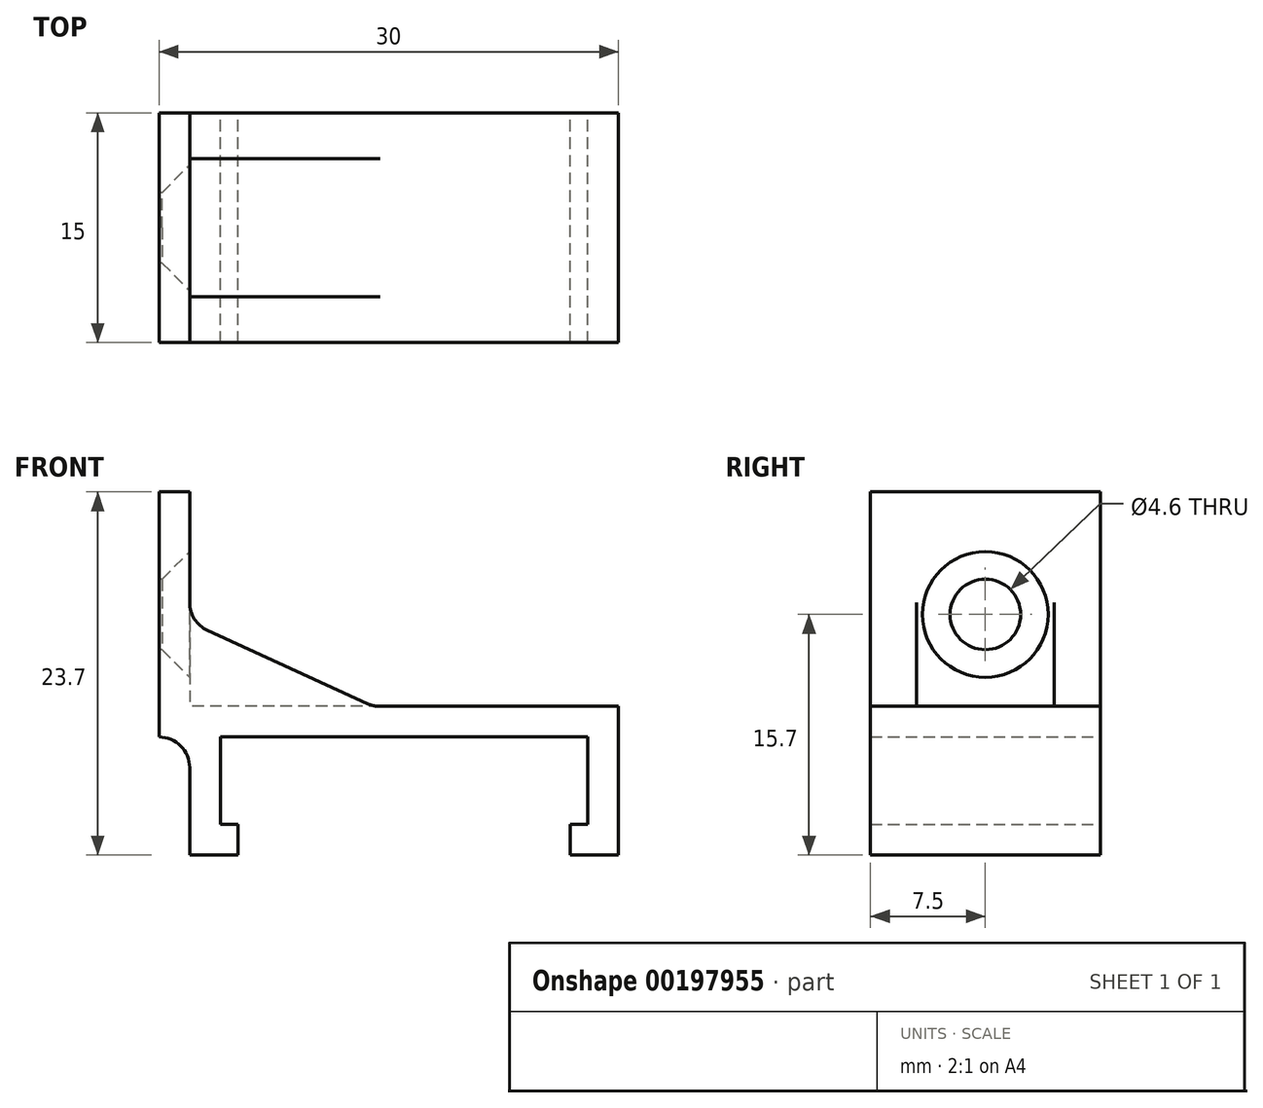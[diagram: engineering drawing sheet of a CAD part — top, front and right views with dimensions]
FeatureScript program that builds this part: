
annotation { "Feature Type Name" : "Feature", "Feature Type Description" : "" }
export const myFeature = defineFeature(function(context is Context, id is Id, definition is map)
    precondition{}
    {
        {
            var Q0;
            Q0=qCreatedBy(makeId("Front.planeOp"),FACE);
            var sketch = newSketch(context, id + "F0", { "sketchPlane" : qUnion([Q0])});
            skLineSegment(sketch, "E0", {"start": v(0, 16) * mm, "end": v(0, 0) * mm});
            skLineSegment(sketch, "E1", {"start": v(2, 0) * mm, "end": v(2, -7.7) * mm});
            skLineSegment(sketch, "E2", {"start": v(2, -7.7) * mm, "end": v(5.15, -7.7) * mm});
            skLineSegment(sketch, "E3", {"start": v(5.15, -7.7) * mm, "end": v(5.15, -5.7) * mm});
            skLineSegment(sketch, "E4", {"start": v(5.15, -5.7) * mm, "end": v(4, -5.7) * mm});
            skLineSegment(sketch, "E5", {"start": v(4, -5.7) * mm, "end": v(4, 0) * mm});
            skLineSegment(sketch, "E6", {"start": v(4, 0) * mm, "end": v(28, 0) * mm});
            skLineSegment(sketch, "E7", {"start": v(28, 0) * mm, "end": v(28, -5.7) * mm});
            skLineSegment(sketch, "E8", {"start": v(28, -5.7) * mm, "end": v(26.85, -5.7) * mm});
            skLineSegment(sketch, "E9", {"start": v(26.85, -5.7) * mm, "end": v(26.85, -7.7) * mm});
            skLineSegment(sketch, "E10", {"start": v(26.85, -7.7) * mm, "end": v(30, -7.7) * mm});
            skLineSegment(sketch, "E11", {"start": v(30, -7.7) * mm, "end": v(30, 2) * mm});
            skLineSegment(sketch, "E12", {"start": v(30, 2) * mm, "end": v(2, 2) * mm});
            skLineSegment(sketch, "E13", {"start": v(2, 16) * mm, "end": v(0, 16) * mm});
            skLineSegment(sketch, "E14", {"start": v(2, 16) * mm, "end": v(2, 2) * mm});
            skLineSegment(sketch, "E15", {"start": v(2, 7.5) * mm, "end": v(14, 2) * mm});
            skLineSegment(sketch, "E16", {"start": v(2, 0) * mm, "end": v(0, 0) * mm});
            skSolve(sketch);
        }
        {
            var Q0;
            Q0=makeQuery(id+"F0.imprint","IMPRINT",FACE,{"disambiguationData":[TD([[makeQuery(id+"F0.imprint","IMPRINT",EDGE,{"derivedFrom":sQuery(id+"F0.wireOp",EDGE,"E0")}),1.0]])]});
            var Q1;
            {var subQ3=sQuery(id+"F0.wireOp",EDGE,"E15");Q1=makeQuery(id+"F0.imprint","IMPRINT",FACE,{"disambiguationData":[TD([[makeQuery(id+"F0.imprint","IMPRINT",EDGE,{"derivedFrom":subQ3}),-1.0]])]});}
            extrude(context, id + "F1", {"entities" : qUnion([Q0, Q1]), "endBound" : BoundingType.SYMMETRIC, "depth" : 15 * mm});
        }
        {
            var Q0;
            {var subQ3=sQuery(id+"F0.wireOp",EDGE,"E15");Q0=makeQuery(id+"F0.imprint","IMPRINT",FACE,{"disambiguationData":[TD([[makeQuery(id+"F0.imprint","IMPRINT",EDGE,{"derivedFrom":subQ3}),-1.0]])]});}
            extrude(context, id + "F2", {"entities" : qUnion([Q0]), "operationType" : NewBodyOperationType.REMOVE, "endBound" : BoundingType.SYMMETRIC, "oppositeDirection" : true, "depth" : 9 * mm});
        }
        {
            var Q0;
            Q0=makeQuery(id+"F1.opExtrude","SWEPT_FACE",FACE,{"disambiguationData":[OSD([sQuery(id+"F0.wireOp",EDGE,"E0")])]});
            var sketch = newSketch(context, id + "F3", { "sketchPlane" : qUnion([Q0])});
            skCircle(sketch, "E17", {"center": v(0, 8) * mm, "radius": 2.3 * mm});
            skPoint(sketch, "E17.centerSnap0", {"position": v(-7.5, 8) * mm});
            skSolve(sketch);
        }
        {
            var Q0;
            Q0=makeQuery(id+"F3.imprint","IMPRINT",FACE,{"disambiguationData":[TD([[makeQuery(id+"F3.imprint","IMPRINT",EDGE,{"derivedFrom":sQuery(id+"F3.wireOp",EDGE,"E17")}),1.0]])]});
            extrude(context, id + "F4", {"entities" : qUnion([Q0]), "operationType" : NewBodyOperationType.REMOVE, "oppositeDirection" : true, "depth" : 5 * mm});
        }
        {
            var Q0;
            {var subQ0=sQuery(id+"F0.wireOp",EDGE,"E14");Q0=makeQuery(id+"F4.boolean.opBoolean","INTERSECT",EDGE,{"derivedFrom":[makeQuery(id+"FJR7jWG7td1IbDr_0.boolean.opBoolean","MERGE",FACE,{"derivedFrom":[makeQuery(id+"F1.opExtrude","SWEPT_FACE",FACE,{"disambiguationData":[OSD([subQ0])]}),makeQuery(id+"FJR7jWG7td1IbDr_0.opExtrude","SWEPT_FACE",FACE,{"disambiguationData":[OSD([subQ0])]})]}),makeQuery(id+"F4.opExtrude","SWEPT_FACE",FACE,{"disambiguationData":[OSD([sQuery(id+"F3.wireOp",EDGE,"E17")])]})]});}
            chamfer(context, id + "F5", {"entities" : qUnion([Q0]), "width" : 1.8 * mm, "tangentPropagation" : true});
        }
        {
            var Q0;
            {var subQ0=sQuery(id+"F0.wireOp",EDGE,"E15");var subQ1=sQuery(id+"F0.wireOp",EDGE,"E14");var subQ2=sQuery(id+"F0.wireOp",EDGE,"E12");Q0=makeQuery(id+"F2.boolean.opBoolean","SPLIT",EDGE,{"disambiguationData":[TD([makeQuery(id+"F2.opExtrude","CAP_FACE",FACE,{"disambiguationData":[OSD([subQ2,subQ1,subQ0])],"isStart":true})])],"derivedFrom":makeQuery(id+"F1.opExtrude","SWEPT_EDGE",EDGE,{"disambiguationData":[OSD([subQ1,subQ0])]})});}
            var Q1;
            {var subQ0=sQuery(id+"F0.wireOp",EDGE,"E12");var subQ1=sQuery(id+"F0.wireOp",EDGE,"E15");var subQ2=sQuery(id+"F0.wireOp",EDGE,"E14");Q1=makeQuery(id+"F2.boolean.opBoolean","SPLIT",EDGE,{"disambiguationData":[TD([makeQuery(id+"F2.opExtrude","CAP_FACE",FACE,{"disambiguationData":[OSD([subQ0,subQ2,subQ1])],"isStart":false})])],"derivedFrom":makeQuery(id+"F1.opExtrude","SWEPT_EDGE",EDGE,{"disambiguationData":[OSD([subQ0,subQ1])]})});}
            var Q2;
            {var subQ0=sQuery(id+"F0.wireOp",EDGE,"E12");var subQ1=sQuery(id+"F0.wireOp",EDGE,"E15");var subQ2=sQuery(id+"F0.wireOp",EDGE,"E14");Q2=makeQuery(id+"F2.boolean.opBoolean","SPLIT",EDGE,{"disambiguationData":[TD([makeQuery(id+"F2.opExtrude","CAP_FACE",FACE,{"disambiguationData":[OSD([subQ0,subQ2,subQ1])],"isStart":true})])],"derivedFrom":makeQuery(id+"F1.opExtrude","SWEPT_EDGE",EDGE,{"disambiguationData":[OSD([subQ0,subQ1])]})});}
            var Q3;
            {var subQ0=sQuery(id+"F0.wireOp",EDGE,"E15");var subQ1=sQuery(id+"F0.wireOp",EDGE,"E14");var subQ2=sQuery(id+"F0.wireOp",EDGE,"E12");Q3=makeQuery(id+"F2.boolean.opBoolean","SPLIT",EDGE,{"disambiguationData":[TD([makeQuery(id+"F2.opExtrude","CAP_FACE",FACE,{"disambiguationData":[OSD([subQ2,subQ1,subQ0])],"isStart":false})])],"derivedFrom":makeQuery(id+"F1.opExtrude","SWEPT_EDGE",EDGE,{"disambiguationData":[OSD([subQ1,subQ0])]})});}
            var Q4;
            Q4=makeQuery(id+"F1.opExtrude","SWEPT_EDGE",EDGE,{"disambiguationData":[OSD([sQuery(id+"F0.wireOp",EDGE,"E1"),sQuery(id+"F0.wireOp",EDGE,"E16")])]});
            fillet(context, id + "F6", {"entities" : qUnion([Q0, Q1, Q2, Q3, Q4]), "radius" : 2 * mm, "tangentPropagation" : true, "allowEdgeOverflow" : false});
        }
    });
